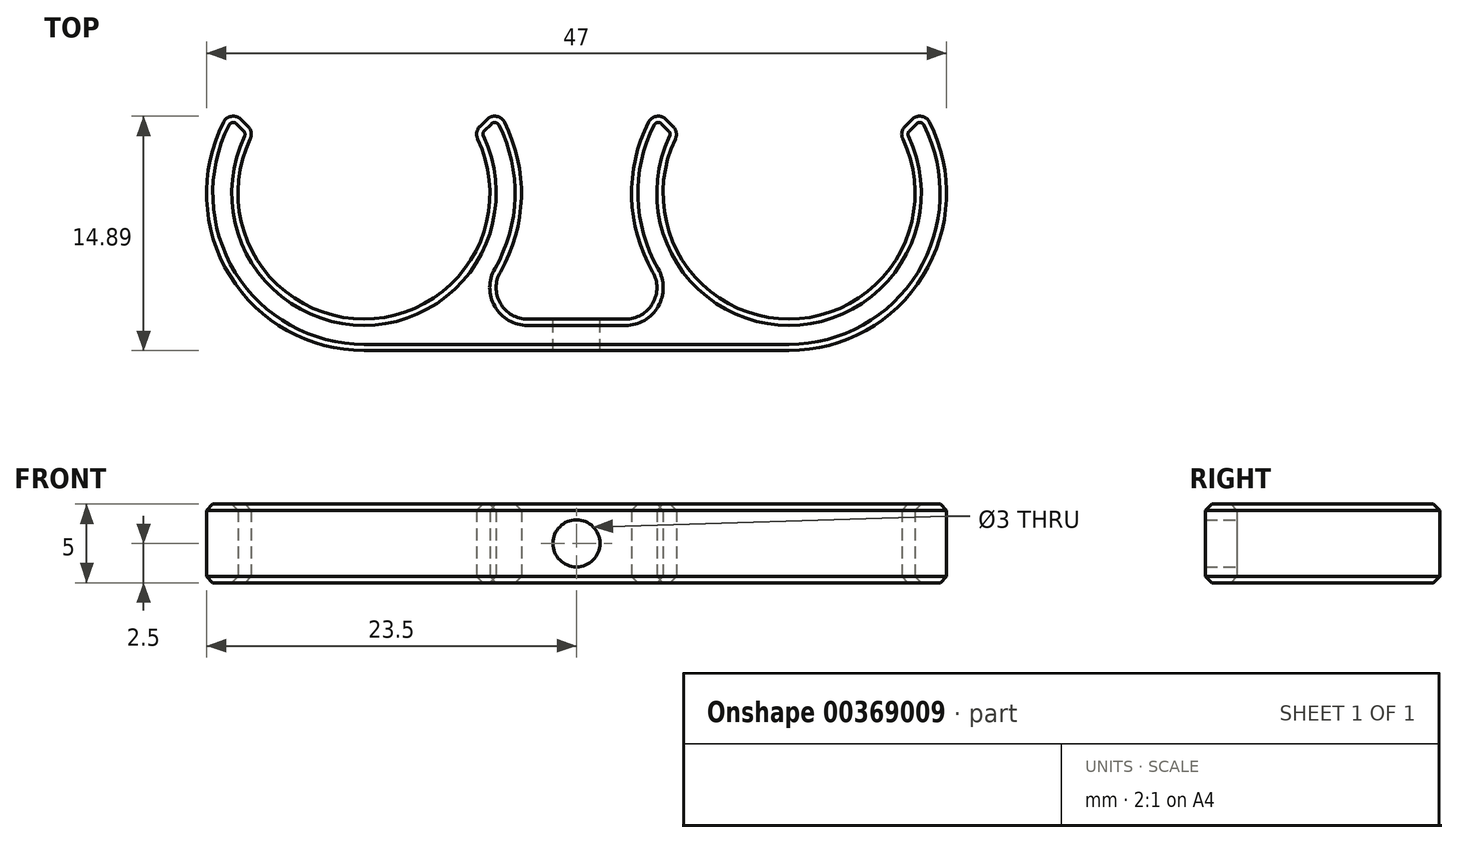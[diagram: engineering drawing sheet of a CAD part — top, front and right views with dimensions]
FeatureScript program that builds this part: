
annotation { "Feature Type Name" : "Feature", "Feature Type Description" : "" }
export const myFeature = defineFeature(function(context is Context, id is Id, definition is map)
    precondition{}
    {
        {
            var Q0;
            Q0=qCreatedBy(makeId("Top.planeOp"),FACE);
            var sketch = newSketch(context, id + "F0", { "sketchPlane" : qUnion([Q0])});
            skCircle(sketch, "E0", {"center": v(13.5, 0) * mm, "radius": 8 * mm, "construction": true});
            skCircle(sketch, "E1", {"center": v(-13.5, 0) * mm, "radius": 8 * mm, "construction": true});
            skArc(sketch, "E2", {"start": v(-6.5, 3.87) * mm, "mid": v(-13.5, -8) * mm, "end": v(-20.5, 3.87) * mm, "construction": true});
            skArc(sketch, "E3", {"start": v(20.5, 3.87) * mm, "mid": v(13.5, -8) * mm, "end": v(6.5, 3.87) * mm, "construction": true});
            skArc(sketch, "E4", {"start": v(-5.04, 5.33) * mm, "mid": v(-13.5, -10) * mm, "end": v(-21.96, 5.33) * mm});
            skArc(sketch, "E5", {"start": v(21.96, 5.33) * mm, "mid": v(13.5, -10) * mm, "end": v(5.04, 5.33) * mm});
            skLineSegment(sketch, "E6", {"start": v(-20.5, 3.87) * mm, "end": v(-21.96, 5.33) * mm});
            skLineSegment(sketch, "E7", {"start": v(-6.5, 3.87) * mm, "end": v(-5.04, 5.33) * mm});
            skLineSegment(sketch, "E8", {"start": v(6.5, 3.87) * mm, "end": v(5.04, 5.33) * mm});
            skLineSegment(sketch, "E9", {"start": v(20.5, 3.87) * mm, "end": v(21.96, 5.33) * mm});
            skLineSegment(sketch, "E10", {"start": v(-13.5, -10) * mm, "end": v(13.5, -10) * mm});
            skLineSegment(sketch, "E11", {"start": v(-7.5, -8) * mm, "end": v(7.5, -8) * mm});
            skArc(sketch, "E12", {"start": v(-6.5, 3.87) * mm, "mid": v(-13.5, -8) * mm, "end": v(-20.5, 3.87) * mm});
            skArc(sketch, "E13", {"start": v(20.5, 3.87) * mm, "mid": v(13.5, -8) * mm, "end": v(6.5, 3.87) * mm});
            skSolve(sketch);
        }
        {
            var Q0;
            {var subQ0=sQuery(id+"F0.wireOp",EDGE,"E6");Q0=makeQuery(id+"F0.imprint","IMPRINT",FACE,{"disambiguationData":[TD([[makeQuery(id+"F0.imprint","IMPRINT",EDGE,{"derivedFrom":subQ0}),1.0]])]});}
            var Q1;
            {var subQ0=sQuery(id+"F0.wireOp",EDGE,"E10");Q1=makeQuery(id+"F0.imprint","IMPRINT",FACE,{"disambiguationData":[TD([[makeQuery(id+"F0.imprint","IMPRINT",EDGE,{"derivedFrom":subQ0}),1.0]])]});}
            var Q2;
            {var subQ0=sQuery(id+"F0.wireOp",EDGE,"E8");Q2=makeQuery(id+"F0.imprint","IMPRINT",FACE,{"disambiguationData":[TD([[makeQuery(id+"F0.imprint","IMPRINT",EDGE,{"derivedFrom":subQ0}),1.0]])]});}
            extrude(context, id + "F1", {"entities" : qUnion([Q0, Q1, Q2]), "depth" : 5 * mm});
        }
        {
            var Q0;
            Q0=makeQuery(id+"F1.opExtrude","SWEPT_EDGE",EDGE,{"disambiguationData":[OSD([sQuery(id+"F0.wireOp",EDGE,"E5"),sQuery(id+"F0.wireOp",EDGE,"E8")])]});
            var Q1;
            Q1=makeQuery(id+"F1.opExtrude","SWEPT_EDGE",EDGE,{"disambiguationData":[OSD([sQuery(id+"F0.wireOp",EDGE,"E8"),sQuery(id+"F0.wireOp",EDGE,"E13")])]});
            var Q2;
            Q2=makeQuery(id+"F1.opExtrude","SWEPT_EDGE",EDGE,{"disambiguationData":[OSD([sQuery(id+"F0.wireOp",EDGE,"E9"),sQuery(id+"F0.wireOp",EDGE,"E13")])]});
            var Q3;
            Q3=makeQuery(id+"F1.opExtrude","SWEPT_EDGE",EDGE,{"disambiguationData":[OSD([sQuery(id+"F0.wireOp",EDGE,"E5"),sQuery(id+"F0.wireOp",EDGE,"E9")])]});
            var Q4;
            Q4=makeQuery(id+"F1.opExtrude","SWEPT_EDGE",EDGE,{"disambiguationData":[OSD([sQuery(id+"F0.wireOp",EDGE,"E4"),sQuery(id+"F0.wireOp",EDGE,"E7")])]});
            var Q5;
            Q5=makeQuery(id+"F1.opExtrude","SWEPT_EDGE",EDGE,{"disambiguationData":[OSD([sQuery(id+"F0.wireOp",EDGE,"E7"),sQuery(id+"F0.wireOp",EDGE,"E12")])]});
            var Q6;
            Q6=makeQuery(id+"F1.opExtrude","SWEPT_EDGE",EDGE,{"disambiguationData":[OSD([sQuery(id+"F0.wireOp",EDGE,"E4"),sQuery(id+"F0.wireOp",EDGE,"E6")])]});
            var Q7;
            Q7=makeQuery(id+"F1.opExtrude","SWEPT_EDGE",EDGE,{"disambiguationData":[OSD([sQuery(id+"F0.wireOp",EDGE,"E6"),sQuery(id+"F0.wireOp",EDGE,"E12")])]});
            fillet(context, id + "F2", {"entities" : qUnion([Q0, Q1, Q2, Q3, Q4, Q5, Q6, Q7]), "radius" : 0.7 * mm, "tangentPropagation" : true, "allowEdgeOverflow" : false});
        }
        {
            var Q0;
            Q0=makeQuery(id+"F1.opExtrude","SWEPT_EDGE",EDGE,{"disambiguationData":[OSD([sQuery(id+"F0.wireOp",EDGE,"E4"),sQuery(id+"F0.wireOp",EDGE,"E11")])]});
            var Q1;
            Q1=makeQuery(id+"F1.opExtrude","SWEPT_EDGE",EDGE,{"disambiguationData":[OSD([sQuery(id+"F0.wireOp",EDGE,"E5"),sQuery(id+"F0.wireOp",EDGE,"E11")])]});
            fillet(context, id + "F3", {"entities" : qUnion([Q0, Q1]), "radius" : 2 * mm, "tangentPropagation" : true, "allowEdgeOverflow" : false});
        }
        {
            var Q0;
            Q0=makeQuery(id+"F1.opExtrude","CAP_FACE",FACE,{"disambiguationData":[OSD([sQuery(id+"F0.wireOp",EDGE,"E4"),sQuery(id+"F0.wireOp",EDGE,"E5"),sQuery(id+"F0.wireOp",EDGE,"E6"),sQuery(id+"F0.wireOp",EDGE,"E7"),sQuery(id+"F0.wireOp",EDGE,"E8"),sQuery(id+"F0.wireOp",EDGE,"E9"),sQuery(id+"F0.wireOp",EDGE,"E10"),sQuery(id+"F0.wireOp",EDGE,"E11"),sQuery(id+"F0.wireOp",EDGE,"E12"),sQuery(id+"F0.wireOp",EDGE,"E13")])],"isStart":true});
            var Q1;
            Q1=makeQuery(id+"F1.opExtrude","CAP_FACE",FACE,{"disambiguationData":[OSD([sQuery(id+"F0.wireOp",EDGE,"E4"),sQuery(id+"F0.wireOp",EDGE,"E5"),sQuery(id+"F0.wireOp",EDGE,"E6"),sQuery(id+"F0.wireOp",EDGE,"E7"),sQuery(id+"F0.wireOp",EDGE,"E8"),sQuery(id+"F0.wireOp",EDGE,"E9"),sQuery(id+"F0.wireOp",EDGE,"E10"),sQuery(id+"F0.wireOp",EDGE,"E11"),sQuery(id+"F0.wireOp",EDGE,"E12"),sQuery(id+"F0.wireOp",EDGE,"E13")])],"isStart":false});
            chamfer(context, id + "F4", {"entities" : qUnion([Q0, Q1]), "width" : 0.4 * mm, "tangentPropagation" : true});
        }
        {
            var Q0;
            Q0=makeQuery(id+"F1.opExtrude","SWEPT_FACE",FACE,{"disambiguationData":[OSD([sQuery(id+"F0.wireOp",EDGE,"E11")])]});
            var sketch = newSketch(context, id + "F5", { "sketchPlane" : qUnion([Q0])});
            skCircle(sketch, "E14", {"center": v(0, 2.5) * mm, "radius": 1.5 * mm});
            skSolve(sketch);
        }
        {
            var Q0;
            Q0=makeQuery(id+"F5.imprint","IMPRINT",FACE,{"disambiguationData":[TD([[makeQuery(id+"F5.imprint","IMPRINT",EDGE,{"derivedFrom":sQuery(id+"F5.wireOp",EDGE,"E14")}),1.0]])]});
            extrude(context, id + "F6", {"entities" : qUnion([Q0]), "operationType" : NewBodyOperationType.REMOVE, "endBound" : BoundingType.THROUGH_ALL, "oppositeDirection" : true, "depth" : 25 * mm});
        }
    });
